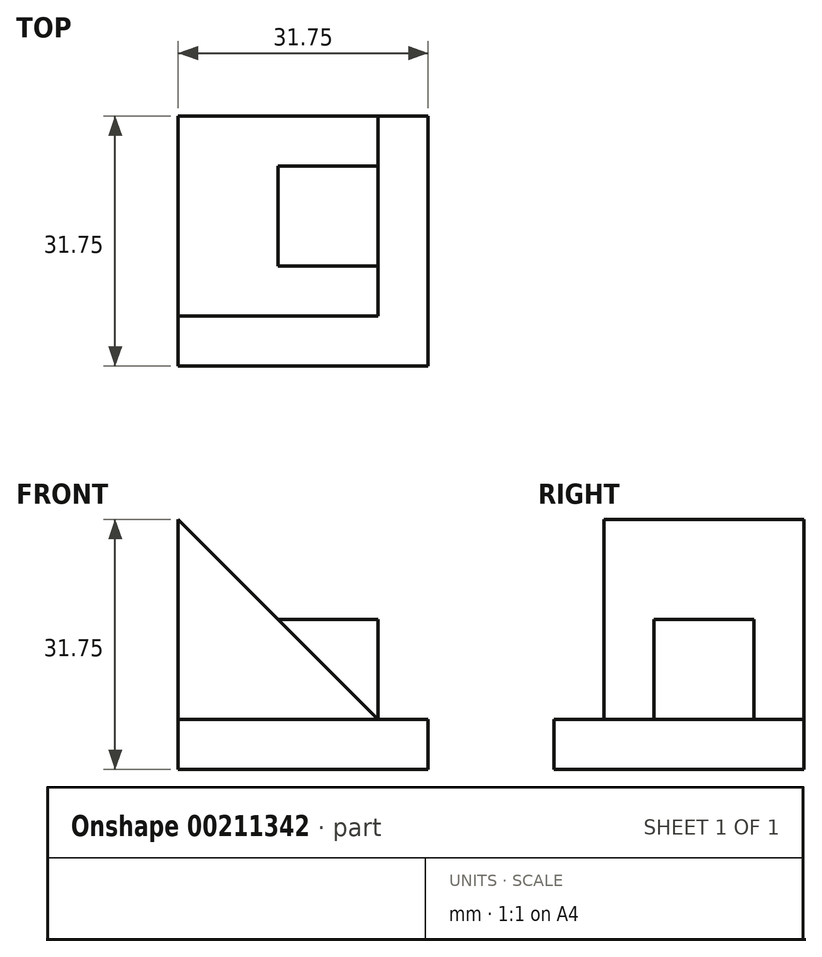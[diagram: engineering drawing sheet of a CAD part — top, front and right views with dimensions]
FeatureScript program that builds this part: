
annotation { "Feature Type Name" : "Feature", "Feature Type Description" : "" }
export const myFeature = defineFeature(function(context is Context, id is Id, definition is map)
    precondition{}
    {
        {
            var Q0;
            Q0=qCreatedBy(makeId("Top.planeOp"),FACE);
            var sketch = newSketch(context, id + "F0", { "sketchPlane" : qUnion([Q0])});
            skLineSegment(sketch, "E0", {"start": v(0, 0) * mm, "end": v(0, 31.75) * mm});
            skLineSegment(sketch, "E1", {"start": v(0, 31.75) * mm, "end": v(31.75, 31.75) * mm});
            skLineSegment(sketch, "E2", {"start": v(31.75, 31.75) * mm, "end": v(31.75, 0) * mm});
            skLineSegment(sketch, "E3", {"start": v(31.75, 0) * mm, "end": v(0, 0) * mm});
            skSolve(sketch);
        }
        {
            var Q0;
            Q0=makeQuery(id+"F0.imprint","IMPRINT",FACE,{"disambiguationData":[TD([[makeQuery(id+"F0.imprint","IMPRINT",EDGE,{"derivedFrom":sQuery(id+"F0.wireOp",EDGE,"E0")}),-1.0]])]});
            extrude(context, id + "F1", {"entities" : qUnion([Q0]), "depth" : 6.35 * mm});
        }
        {
            var Q0;
            Q0=makeQuery(id+"F1.opExtrude","SWEPT_FACE",FACE,{"disambiguationData":[OSD([sQuery(id+"F0.wireOp",EDGE,"E1")])]});
            var sketch = newSketch(context, id + "F2", { "sketchPlane" : qUnion([Q0])});
            skLineSegment(sketch, "E4", {"start": v(0, 6.35) * mm, "end": v(0, 31.75) * mm});
            skLineSegment(sketch, "E5", {"start": v(0, 6.35) * mm, "end": v(-25.4, 6.35) * mm});
            skLineSegment(sketch, "E6", {"start": v(0, 31.75) * mm, "end": v(-25.4, 6.35) * mm});
            skSolve(sketch);
        }
        {
            var Q0;
            Q0=makeQuery(id+"F2.imprint","IMPRINT",FACE,{"disambiguationData":[TD([[makeQuery(id+"F2.imprint","IMPRINT",EDGE,{"derivedFrom":sQuery(id+"F2.wireOp",EDGE,"E4")}),1.0]])]});
            extrude(context, id + "F3", {"entities" : qUnion([Q0]), "operationType" : NewBodyOperationType.ADD, "oppositeDirection" : true, "depth" : 25.4 * mm});
        }
        {
            var Q0;
            Q0=makeQuery(id+"F3.boolean.opBoolean","MERGE",FACE,{"derivedFrom":[makeQuery(id+"F1.opExtrude","SWEPT_FACE",FACE,{"disambiguationData":[OSD([sQuery(id+"F0.wireOp",EDGE,"E1")])]}),makeQuery(id+"F3.opExtrude","CAP_FACE",FACE,{"disambiguationData":[OSD([sQuery(id+"F2.wireOp",EDGE,"E4"),sQuery(id+"F2.wireOp",EDGE,"E5"),sQuery(id+"F2.wireOp",EDGE,"E6")])],"isStart":true})]});
            var sketch = newSketch(context, id + "F4", { "sketchPlane" : qUnion([Q0])});
            skLineSegment(sketch, "E7", {"start": v(-25.4, 6.35) * mm, "end": v(-25.4, 19.05) * mm});
            skLineSegment(sketch, "E8", {"start": v(-25.4, 19.05) * mm, "end": v(-12.7, 19.05) * mm});
            skSolve(sketch);
        }
        {
            var Q0;
            {var subQ0=sQuery(id+"F4.wireOp",EDGE,"E7");Q0=makeQuery(id+"F4.imprint","IMPRINT",FACE,{"disambiguationData":[TD([[makeQuery(id+"F4.imprint","IMPRINT",EDGE,{"derivedFrom":subQ0}),-1.0]])]});}
            extrude(context, id + "F5", {"entities" : qUnion([Q0]), "operationType" : NewBodyOperationType.ADD, "oppositeDirection" : true, "depth" : 19.05 * mm});
        }
        {
            var Q0;
            {var subQ0=sQuery(id+"F2.wireOp",EDGE,"E6");Q0=makeQuery(id+"F5.boolean.opBoolean","MERGE",FACE,{"derivedFrom":[makeQuery(id+"F3.boolean.opBoolean","MERGE",FACE,{"derivedFrom":[makeQuery(id+"F1.opExtrude","SWEPT_FACE",FACE,{"disambiguationData":[OSD([sQuery(id+"F0.wireOp",EDGE,"E1")])]}),makeQuery(id+"F3.opExtrude","CAP_FACE",FACE,{"disambiguationData":[OSD([sQuery(id+"F2.wireOp",EDGE,"E4"),sQuery(id+"F2.wireOp",EDGE,"E5"),subQ0])],"isStart":true})]}),makeQuery(id+"F5.opExtrude","CAP_FACE",FACE,{"disambiguationData":[OSD([subQ0,sQuery(id+"F4.wireOp",EDGE,"E7"),sQuery(id+"F4.wireOp",EDGE,"E8")])],"isStart":true})]});}
            var sketch = newSketch(context, id + "F6", { "sketchPlane" : qUnion([Q0])});
            skLineSegment(sketch, "E9", {"start": v(-25.4, 6.35) * mm, "end": v(-12.7, 19.05) * mm});
            skLineSegment(sketch, "E10", {"start": v(-12.7, 19.05) * mm, "end": v(-25.4, 19.05) * mm});
            skLineSegment(sketch, "E11", {"start": v(-25.4, 19.05) * mm, "end": v(-25.4, 6.35) * mm});
            skSolve(sketch);
        }
        {
            var Q0;
            Q0=makeQuery(id+"F6.imprint","IMPRINT",FACE,{"disambiguationData":[TD([[makeQuery(id+"F6.imprint","IMPRINT",EDGE,{"derivedFrom":sQuery(id+"F6.wireOp",EDGE,"E9")}),1.0]])]});
            extrude(context, id + "F7", {"entities" : qUnion([Q0]), "operationType" : NewBodyOperationType.REMOVE, "oppositeDirection" : true, "depth" : 6.35 * mm});
        }
    });
